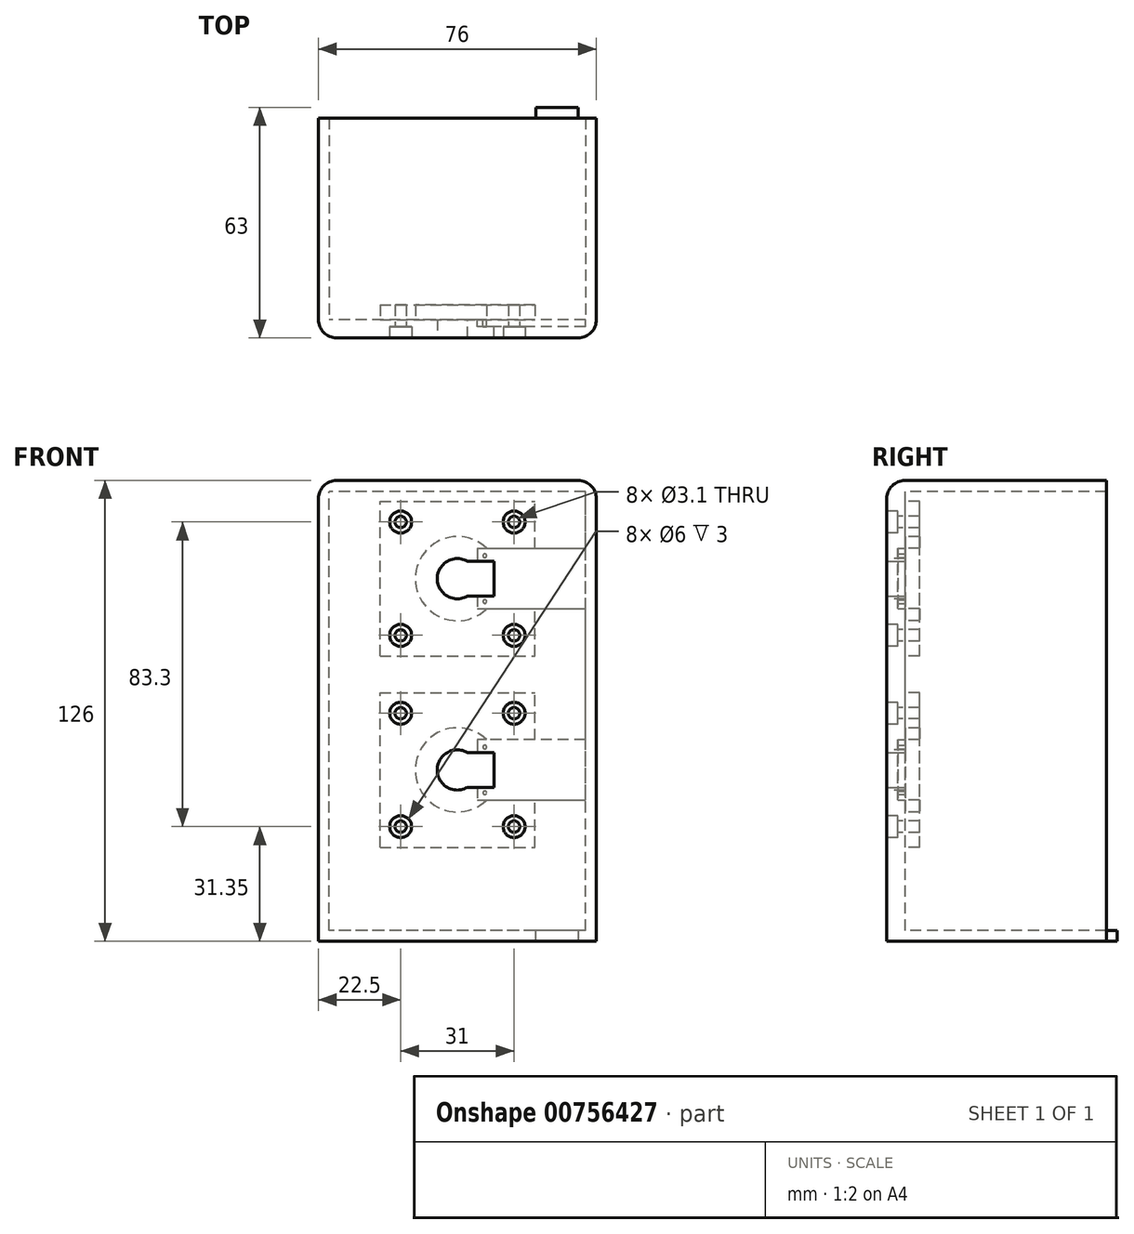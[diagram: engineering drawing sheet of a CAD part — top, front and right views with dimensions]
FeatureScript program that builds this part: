
annotation { "Feature Type Name" : "Feature", "Feature Type Description" : "" }
export const myFeature = defineFeature(function(context is Context, id is Id, definition is map)
    precondition{}
    {
        {
            var Q0;
            Q0=qCreatedBy(makeId("Front.planeOp"),FACE);
            var sketch = newSketch(context, id + "F0", { "sketchPlane" : qUnion([Q0])});
            skLineSegment(sketch, "E0.bottom", {"start": v(-21.15, 15) * mm, "end": v(21.15, 15) * mm, "construction": true});
            skLineSegment(sketch, "E0.top", {"start": v(-21.15, 57.3) * mm, "end": v(21.15, 57.3) * mm, "construction": true});
            skLineSegment(sketch, "E0.left", {"start": v(-21.15, 15) * mm, "end": v(-21.15, 57.3) * mm, "construction": true});
            skLineSegment(sketch, "E0.right", {"start": v(21.15, 15) * mm, "end": v(21.15, 57.3) * mm, "construction": true});
            skPoint(sketch, "E0.middle", {"position": v(0, 36.15) * mm});
            skLineSegment(sketch, "E1.bottom", {"start": v(21.15, -37.3) * mm, "end": v(-21.15, -37.3) * mm, "construction": true});
            skLineSegment(sketch, "E1.top", {"start": v(21.15, 5) * mm, "end": v(-21.15, 5) * mm, "construction": true});
            skLineSegment(sketch, "E1.left", {"start": v(21.15, -37.3) * mm, "end": v(21.15, 5) * mm, "construction": true});
            skLineSegment(sketch, "E1.right", {"start": v(-21.15, -37.3) * mm, "end": v(-21.15, 5) * mm, "construction": true});
            skPoint(sketch, "E1.middle", {"position": v(0, -16.15) * mm});
            skCircle(sketch, "E2", {"center": v(0, -16.15) * mm, "radius": 11.5 * mm, "construction": true});
            skCircle(sketch, "E3", {"center": v(0, 36.15) * mm, "radius": 11.5 * mm, "construction": true});
            skPoint(sketch, "E4", {"position": v(15.5, 51.65) * mm});
            skPoint(sketch, "E5", {"position": v(15.5, 20.65) * mm});
            skPoint(sketch, "E6", {"position": v(15.5, -0.65) * mm});
            skPoint(sketch, "E7", {"position": v(15.5, -31.65) * mm});
            skPoint(sketch, "E8", {"position": v(-15.5, -31.65) * mm});
            skPoint(sketch, "E9", {"position": v(-15.5, -0.65) * mm});
            skPoint(sketch, "E10", {"position": v(-15.5, 20.65) * mm});
            skPoint(sketch, "E11", {"position": v(-15.5, 51.65) * mm});
            skLineSegment(sketch, "E12", {"start": v(-5.14, 36.15) * mm, "end": v(4.92, 36.15) * mm, "construction": true});
            skLineSegment(sketch, "E13", {"start": v(-4.7, -16.15) * mm, "end": v(5.14, -16.15) * mm, "construction": true});
            skLineSegment(sketch, "E14.bottom", {"start": v(35, -60) * mm, "end": v(-35, -60) * mm});
            skLineSegment(sketch, "E14.top", {"start": v(35, 60) * mm, "end": v(-35, 60) * mm});
            skLineSegment(sketch, "E14.left", {"start": v(35, -60) * mm, "end": v(35, 60) * mm});
            skLineSegment(sketch, "E14.right", {"start": v(-35, -60) * mm, "end": v(-35, 60) * mm});
            skPoint(sketch, "E14.middle", {"position": v(0, 0) * mm});
            skCircle(sketch, "E15", {"center": v(0, 36.15) * mm, "radius": 5.5 * mm});
            skCircle(sketch, "E16", {"center": v(0, -16.15) * mm, "radius": 5.5 * mm});
            skLineSegment(sketch, "E17", {"start": v(-38, 63) * mm, "end": v(-38, -63) * mm});
            skLineSegment(sketch, "E18", {"start": v(-38, -63) * mm, "end": v(38, -63) * mm});
            skLineSegment(sketch, "E19", {"start": v(-38, 63) * mm, "end": v(38, 63) * mm});
            skLineSegment(sketch, "E20", {"start": v(38, 63) * mm, "end": v(38, -63) * mm});
            skSolve(sketch);
        }
        {
            var Q0;
            Q0=makeQuery(id+"F0.imprint","IMPRINT",FACE,{"disambiguationData":[TD([[makeQuery(id+"F0.imprint","IMPRINT",EDGE,{"derivedFrom":sQuery(id+"F0.wireOp",EDGE,"E14.bottom")}),-1.0]])]});
            extrude(context, id + "F1", {"entities" : qUnion([Q0]), "oppositeDirection" : true, "depth" : 5 * mm, "offsetDistance" : 25 * mm});
        }
        {
            var Q0;
            Q0=sQuery(id+"F0.wireOp",VERTEX,"E4");
            var Q1;
            Q1=sQuery(id+"F0.wireOp",VERTEX,"E11");
            var Q2;
            Q2=sQuery(id+"F0.wireOp",VERTEX,"E10");
            var Q3;
            Q3=sQuery(id+"F0.wireOp",VERTEX,"E5");
            var Q4;
            Q4=sQuery(id+"F0.wireOp",VERTEX,"E6");
            var Q5;
            Q5=sQuery(id+"F0.wireOp",VERTEX,"E9");
            var Q6;
            Q6=sQuery(id+"F0.wireOp",VERTEX,"E8");
            var Q7;
            Q7=sQuery(id+"F0.wireOp",VERTEX,"E7");
            var Q8;
            Q8=makeQuery(id+"F1.opExtrude","SWEPT_BODY",BODY,{"disambiguationData":[OSD([sQuery(id+"F0.wireOp",EDGE,"E2"),sQuery(id+"F0.wireOp",EDGE,"E3"),sQuery(id+"F0.wireOp",EDGE,"E14.bottom"),sQuery(id+"F0.wireOp",EDGE,"E14.top"),sQuery(id+"F0.wireOp",EDGE,"E14.left"),sQuery(id+"F0.wireOp",EDGE,"E14.right")])]});
            hole(context, id + "F2", {"style" : HoleStyle.C_BORE, "endStyle" : HoleEndStyle.BLIND, "holeDiameter" : 3.1 * mm, "cBoreDiameter" : 6 * mm, "cBoreDepth" : 3 * mm, "majorDiameter" : 5 * mm, "holeDepth" : 5 * mm, "isTappedThrough" : true, "tappedDepth" : 12 * mm, "tapClearance" : 3, "locations" : qUnion([Q0, Q1, Q2, Q3, Q4, Q5, Q6, Q7]), "scope" : qUnion([Q8])});
        }
        {
            var Q0;
            Q0=makeQuery(id+"F1.opExtrude","CAP_FACE",FACE,{"disambiguationData":[OSD([sQuery(id+"F0.wireOp",EDGE,"E2"),sQuery(id+"F0.wireOp",EDGE,"E3"),sQuery(id+"F0.wireOp",EDGE,"E14.bottom"),sQuery(id+"F0.wireOp",EDGE,"E14.top"),sQuery(id+"F0.wireOp",EDGE,"E14.left"),sQuery(id+"F0.wireOp",EDGE,"E14.right")])],"isStart":false});
            var sketch = newSketch(context, id + "F3", { "sketchPlane" : qUnion([Q0])});
            skCircle(sketch, "E21", {"center": v(0, 36.15) * mm, "radius": 11.5 * mm});
            skLineSegment(sketch, "E22", {"start": v(-8.01, 44.4) * mm, "end": v(-35, 44.4) * mm});
            skLineSegment(sketch, "E23", {"start": v(-8.01, 27.9) * mm, "end": v(-35, 27.9) * mm});
            skLineSegment(sketch, "E24", {"start": v(-35, 44.4) * mm, "end": v(-35, 27.9) * mm});
            skLineSegment(sketch, "E25", {"start": v(-8.01, 44.4) * mm, "end": v(-5.5, 44.4) * mm});
            skLineSegment(sketch, "E26", {"start": v(-5.5, 44.4) * mm, "end": v(-5.5, 40.9) * mm});
            skLineSegment(sketch, "E27", {"start": v(-10, 40.9) * mm, "end": v(-10, 31.4) * mm});
            skLineSegment(sketch, "E28", {"start": v(-5.5, 31.4) * mm, "end": v(-5.5, 27.9) * mm});
            skLineSegment(sketch, "E29", {"start": v(-5.5, 27.9) * mm, "end": v(-8.01, 27.9) * mm});
            skPoint(sketch, "E30", {"position": v(-7.5, 42.4) * mm});
            skPoint(sketch, "E31", {"position": v(-7.5, 29.9) * mm});
            skLineSegment(sketch, "E32", {"start": v(-10, 40.9) * mm, "end": v(2.77, 40.9) * mm});
            skLineSegment(sketch, "E33", {"start": v(-10, 31.4) * mm, "end": v(-2.77, 31.4) * mm});
            skCircle(sketch, "E34", {"center": v(-7.5, 42.4) * mm, "radius": 0.5 * mm});
            skCircle(sketch, "E35", {"center": v(-7.5, 29.9) * mm, "radius": 0.5 * mm});
            skLineSegment(sketch, "E36.bottom", {"start": v(21.15, 15) * mm, "end": v(-21.15, 15) * mm});
            skLineSegment(sketch, "E36.top", {"start": v(21.15, 57.3) * mm, "end": v(-21.15, 57.3) * mm});
            skLineSegment(sketch, "E36.left", {"start": v(21.15, 15) * mm, "end": v(21.15, 57.3) * mm});
            skLineSegment(sketch, "E36.right", {"start": v(-21.15, 15) * mm, "end": v(-21.15, 57.3) * mm});
            skCircle(sketch, "E37", {"center": v(0, -16.15) * mm, "radius": 11.5 * mm});
            skLineSegment(sketch, "E38.bottom", {"start": v(21.15, -37.3) * mm, "end": v(-21.15, -37.3) * mm});
            skLineSegment(sketch, "E38.top", {"start": v(21.15, 5) * mm, "end": v(-21.15, 5) * mm});
            skLineSegment(sketch, "E38.left", {"start": v(21.15, -37.3) * mm, "end": v(21.15, 5) * mm});
            skLineSegment(sketch, "E38.right", {"start": v(-21.15, -37.3) * mm, "end": v(-21.15, 5) * mm});
            skLineSegment(sketch, "E39", {"start": v(-35, -7.9) * mm, "end": v(-5.5, -7.9) * mm});
            skLineSegment(sketch, "E40", {"start": v(-5.5, -7.9) * mm, "end": v(-5.5, -11.4) * mm});
            skLineSegment(sketch, "E41", {"start": v(-5.5, -11.4) * mm, "end": v(-10, -11.4) * mm});
            skLineSegment(sketch, "E42", {"start": v(-10, -11.4) * mm, "end": v(-10, -20.9) * mm});
            skLineSegment(sketch, "E43", {"start": v(-10, -20.9) * mm, "end": v(-5.5, -20.9) * mm});
            skLineSegment(sketch, "E44", {"start": v(-5.5, -20.9) * mm, "end": v(-5.5, -24.4) * mm});
            skLineSegment(sketch, "E45", {"start": v(-5.5, -24.4) * mm, "end": v(-35, -24.4) * mm});
            skLineSegment(sketch, "E46", {"start": v(-35, -24.4) * mm, "end": v(-35, -7.9) * mm});
            skCircle(sketch, "E47", {"center": v(-7.5, -9.9) * mm, "radius": 0.5 * mm});
            skCircle(sketch, "E48", {"center": v(-7.5, -22.4) * mm, "radius": 0.5 * mm});
            skPoint(sketch, "E48.perimeterSnap0", {"position": v(-5.5, -22.65) * mm});
            skPoint(sketch, "E48.perimeterSnap1", {"position": v(-7.75, -11.4) * mm});
            skLineSegment(sketch, "E49", {"start": v(-5.5, -11.4) * mm, "end": v(2.77, -11.4) * mm});
            skLineSegment(sketch, "E50", {"start": v(-5.5, -20.9) * mm, "end": v(-2.77, -20.9) * mm});
            skSolve(sketch);
        }
        {
            var Q0;
            {var subQ0=sQuery(id+"F3.wireOp",EDGE,"E22");Q0=makeQuery(id+"F3.imprint","IMPRINT",FACE,{"disambiguationData":[TD([[makeQuery(id+"F3.imprint","IMPRINT",EDGE,{"derivedFrom":subQ0}),1.0]])]});}
            var Q1;
            {var subQ2=sQuery(id+"F3.wireOp",EDGE,"E25");Q1=makeQuery(id+"F3.imprint","IMPRINT",FACE,{"disambiguationData":[TD([[makeQuery(id+"F3.imprint","IMPRINT",EDGE,{"derivedFrom":subQ2}),-1.0]])]});}
            var Q2;
            {var subQ5=sQuery(id+"F3.wireOp",EDGE,"E46");Q2=makeQuery(id+"F3.imprint","IMPRINT",FACE,{"disambiguationData":[TD([[makeQuery(id+"F3.imprint","IMPRINT",EDGE,{"derivedFrom":subQ5}),-1.0]])]});}
            var Q3;
            {var subQ0=sQuery(id+"F3.wireOp",EDGE,"E39");var subQ1=sQuery(id+"F3.wireOp",EDGE,"E37");var subQ2=makeQuery(id+"F3.imprint","INTERSECT",VERTEX,{"derivedFrom":[subQ1,subQ0]});Q3=makeQuery(id+"F3.imprint","IMPRINT",FACE,{"disambiguationData":[TD([[makeQuery(id+"F3.imprint","IMPRINT",EDGE,{"disambiguationData":[TD([[subQ2,-1.0]])],"derivedFrom":subQ1}),-1.0]])]});}
            var Q4;
            {var subQ0=sQuery(id+"F3.wireOp",EDGE,"E40");Q4=makeQuery(id+"F3.imprint","IMPRINT",FACE,{"disambiguationData":[TD([[makeQuery(id+"F3.imprint","IMPRINT",EDGE,{"derivedFrom":subQ0}),-1.0]])]});}
            extrude(context, id + "F4", {"entities" : qUnion([Q0, Q1, Q2, Q3, Q4]), "operationType" : NewBodyOperationType.REMOVE, "oppositeDirection" : true, "depth" : 2 * mm, "offsetDistance" : 25 * mm});
        }
        {
            var Q0;
            {var subQ4=sQuery(id+"F3.wireOp",EDGE,"E27");Q0=makeQuery(id+"F3.imprint","IMPRINT",FACE,{"disambiguationData":[TD([[makeQuery(id+"F3.imprint","IMPRINT",EDGE,{"derivedFrom":subQ4}),1.0]])]});}
            var Q1;
            Q1=makeQuery(id+"F3.imprint","IMPRINT",FACE,{"disambiguationData":[TD([[makeQuery(id+"F3.imprint","IMPRINT",EDGE,{"derivedFrom":sQuery(id+"F3.wireOp",EDGE,"E41")}),1.0]])]});
            extrude(context, id + "F5", {"entities" : qUnion([Q0, Q1]), "operationType" : NewBodyOperationType.REMOVE, "oppositeDirection" : true, "depth" : 5 * mm, "offsetDistance" : 25 * mm});
        }
        {
            var Q0;
            {var subQ1=sQuery(id+"F3.wireOp",EDGE,"E36.bottom");Q0=makeQuery(id+"F3.imprint","IMPRINT",FACE,{"disambiguationData":[TD([[makeQuery(id+"F3.imprint","IMPRINT",EDGE,{"derivedFrom":subQ1}),-1.0]])]});}
            var Q1;
            {var subQ9=sQuery(id+"F3.wireOp",EDGE,"E38.bottom");Q1=makeQuery(id+"F3.imprint","IMPRINT",FACE,{"disambiguationData":[TD([[makeQuery(id+"F3.imprint","IMPRINT",EDGE,{"derivedFrom":subQ9}),-1.0]])]});}
            extrude(context, id + "F6", {"entities" : qUnion([Q0, Q1]), "operationType" : NewBodyOperationType.ADD, "depth" : 4 * mm, "offsetDistance" : 25 * mm});
        }
        {
            var Q0;
            Q0=makeQuery(id+"F0.imprint","IMPRINT",FACE,{"disambiguationData":[TD([[makeQuery(id+"F0.imprint","IMPRINT",EDGE,{"derivedFrom":sQuery(id+"F0.wireOp",EDGE,"E14.bottom")}),1.0]])]});
            extrude(context, id + "F7", {"entities" : qUnion([Q0]), "operationType" : NewBodyOperationType.ADD, "oppositeDirection" : true, "depth" : 60 * mm, "offsetDistance" : 25 * mm});
        }
        {
            var Q0;
            Q0=makeQuery(id+"F7.opExtrude","SWEPT_EDGE",EDGE,{"disambiguationData":[OSD([sQuery(id+"F0.wireOp",EDGE,"E19"),sQuery(id+"F0.wireOp",EDGE,"E20")])]});
            var Q1;
            Q1=makeQuery(id+"F7.opExtrude","CAP_EDGE",EDGE,{"disambiguationData":[OSD([sQuery(id+"F0.wireOp",EDGE,"E20")])],"isStart":true});
            var Q2;
            Q2=makeQuery(id+"F7.opExtrude","CAP_EDGE",EDGE,{"disambiguationData":[OSD([sQuery(id+"F0.wireOp",EDGE,"E19")])],"isStart":true});
            var Q3;
            Q3=makeQuery(id+"F7.opExtrude","SWEPT_EDGE",EDGE,{"disambiguationData":[OSD([sQuery(id+"F0.wireOp",EDGE,"E17"),sQuery(id+"F0.wireOp",EDGE,"E19")])]});
            var Q4;
            Q4=makeQuery(id+"F7.opExtrude","CAP_EDGE",EDGE,{"disambiguationData":[OSD([sQuery(id+"F0.wireOp",EDGE,"E17")])],"isStart":true});
            fillet(context, id + "F8", {"entities" : qUnion([Q0, Q1, Q2, Q3, Q4]), "radius" : 5 * mm, "tangentPropagation" : true, "allowEdgeOverflow" : false});
        }
        {
            var Q0;
            Q0=makeQuery(id+"F7.opExtrude","CAP_FACE",FACE,{"disambiguationData":[OSD([sQuery(id+"F0.wireOp",EDGE,"E14.bottom"),sQuery(id+"F0.wireOp",EDGE,"E14.top"),sQuery(id+"F0.wireOp",EDGE,"E14.left"),sQuery(id+"F0.wireOp",EDGE,"E14.right"),sQuery(id+"F0.wireOp",EDGE,"E17"),sQuery(id+"F0.wireOp",EDGE,"E18"),sQuery(id+"F0.wireOp",EDGE,"E19"),sQuery(id+"F0.wireOp",EDGE,"E20")])],"isStart":false});
            var sketch = newSketch(context, id + "F9", { "sketchPlane" : qUnion([Q0])});
            skLineSegment(sketch, "E51", {"start": v(-33, -60) * mm, "end": v(-33, -63) * mm});
            skLineSegment(sketch, "E52", {"start": v(-21.5, -63) * mm, "end": v(-21.5, -60) * mm});
            skSolve(sketch);
        }
        {
            var Q0;
            {var subQ0=sQuery(id+"F9.wireOp",EDGE,"E51");Q0=makeQuery(id+"F9.imprint","IMPRINT",FACE,{"disambiguationData":[TD([[makeQuery(id+"F9.imprint","IMPRINT",EDGE,{"derivedFrom":subQ0}),1.0]])]});}
            extrude(context, id + "F10", {"entities" : qUnion([Q0]), "operationType" : NewBodyOperationType.ADD, "depth" : 3 * mm, "offsetDistance" : 25 * mm});
        }
    });
